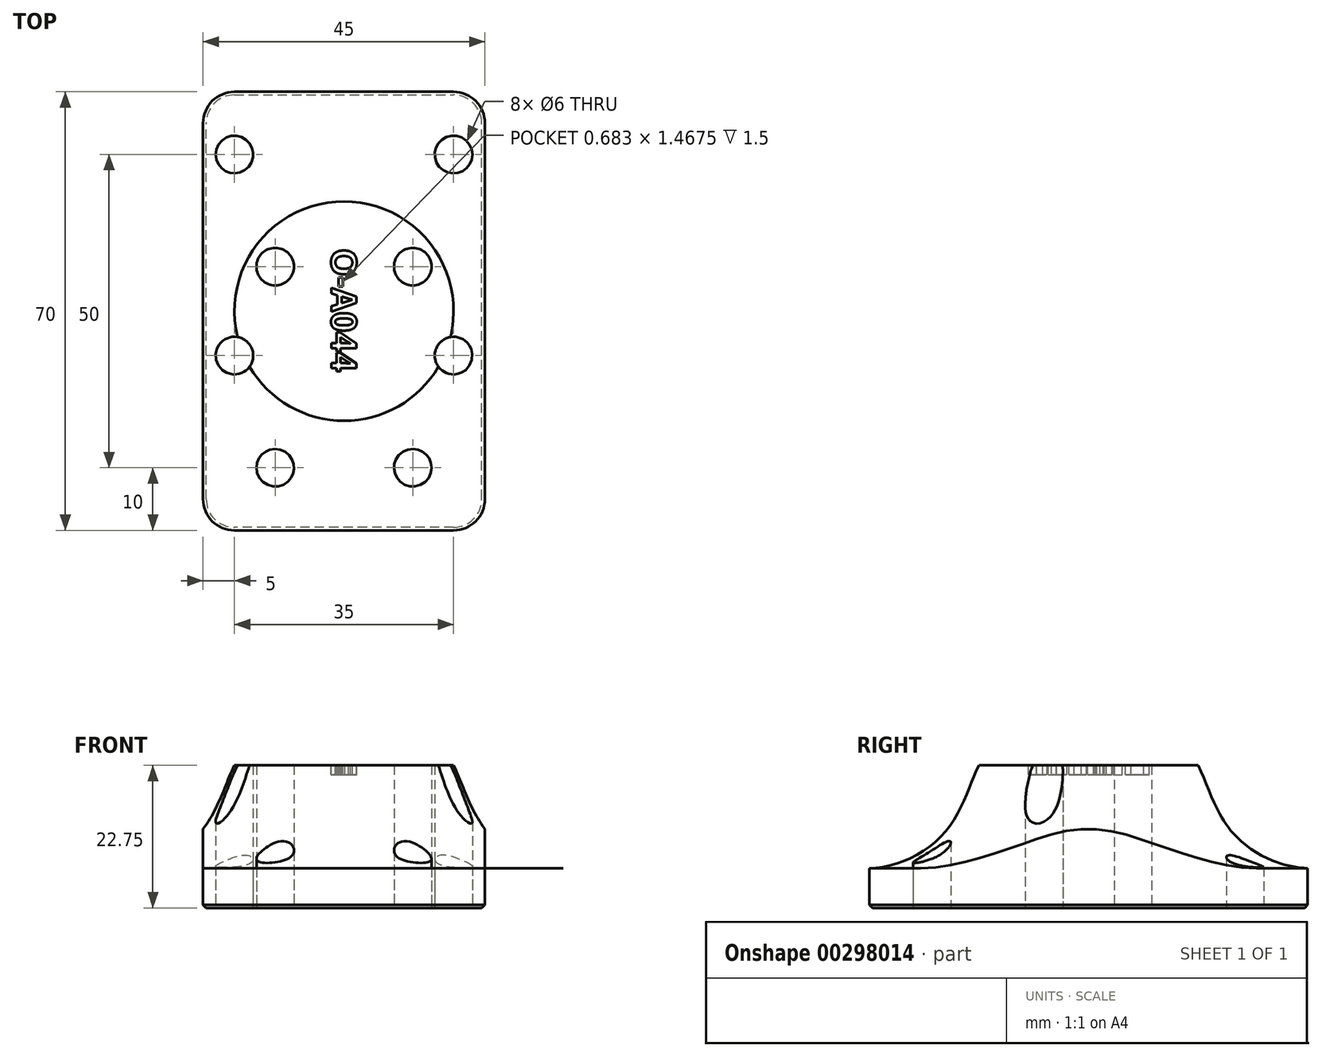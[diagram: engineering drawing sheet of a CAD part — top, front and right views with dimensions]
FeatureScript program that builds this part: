
annotation { "Feature Type Name" : "Feature", "Feature Type Description" : "" }
export const myFeature = defineFeature(function(context is Context, id is Id, definition is map)
    precondition{}
    {
        {
            var Q0;
            Q0=qCreatedBy(makeId("Top.planeOp"),FACE);
            var sketch = newSketch(context, id + "F0", { "sketchPlane" : qUnion([Q0])});
            skLineSegment(sketch, "E0.bottom", {"start": v(-22.5, 35) * mm, "end": v(22.5, 35) * mm});
            skLineSegment(sketch, "E0.top", {"start": v(-22.5, -35) * mm, "end": v(22.5, -35) * mm});
            skLineSegment(sketch, "E0.left", {"start": v(-22.5, 35) * mm, "end": v(-22.5, -35) * mm});
            skLineSegment(sketch, "E0.right", {"start": v(22.5, 35) * mm, "end": v(22.5, -35) * mm});
            skPoint(sketch, "E0.middle", {"position": v(0, 0) * mm});
            skCircle(sketch, "E1", {"center": v(-10.98, 7.1) * mm, "radius": 3 * mm});
            skCircle(sketch, "E2", {"center": v(-17.5, 25) * mm, "radius": 3 * mm});
            skLineSegment(sketch, "E3", {"start": v(-17.5, 25) * mm, "end": v(-10.98, 7.1) * mm, "construction": true});
            skCircle(sketch, "E4", {"center": v(-10.98, -25) * mm, "radius": 3 * mm});
            skCircle(sketch, "E5", {"center": v(-17.5, -7.1) * mm, "radius": 3 * mm});
            skLineSegment(sketch, "E6", {"start": v(-17.5, -7.1) * mm, "end": v(0, -7.1) * mm, "construction": true});
            skLineSegment(sketch, "E7", {"start": v(-17.5, -7.1) * mm, "end": v(-10.98, -25) * mm, "construction": true});
            skLineSegment(sketch, "E8", {"start": v(-17.5, 25) * mm, "end": v(-22.5, 25) * mm, "construction": true});
            skCircle(sketch, "E9.MirrorC", {"center": v(17.5, 25) * mm, "radius": 3 * mm});
            skCircle(sketch, "E10.MirrorC", {"center": v(10.98, 7.1) * mm, "radius": 3 * mm});
            skCircle(sketch, "E11.MirrorC", {"center": v(17.5, -7.1) * mm, "radius": 3 * mm});
            skCircle(sketch, "E12.MirrorC", {"center": v(10.98, -25) * mm, "radius": 3 * mm});
            skLineSegment(sketch, "E13", {"start": v(0, 35) * mm, "end": v(0, -35) * mm});
            skSolve(sketch);
        }
        {
            var Q0;
            {var subQ0=sQuery(id+"F0.wireOp",EDGE,"E0.left");Q0=makeQuery(id+"F0.imprint","IMPRINT",FACE,{"disambiguationData":[TD([[makeQuery(id+"F0.imprint","IMPRINT",EDGE,{"derivedFrom":subQ0}),1.0]])]});}
            extrude(context, id + "F1", {"entities" : qUnion([Q0]), "depth" : 22.75 * mm});
        }
        {
            var Q0;
            Q0=makeQuery(id+"F1.opExtrude","SWEPT_EDGE",EDGE,{"disambiguationData":[OSD([sQuery(id+"F0.wireOp",EDGE,"E0.top"),sQuery(id+"F0.wireOp",EDGE,"E0.left")])]});
            var Q1;
            Q1=makeQuery(id+"F1.opExtrude","SWEPT_EDGE",EDGE,{"disambiguationData":[OSD([sQuery(id+"F0.wireOp",EDGE,"E0.bottom"),sQuery(id+"F0.wireOp",EDGE,"E0.left")])]});
            fillet(context, id + "F2", {"entities" : qUnion([Q0, Q1]), "radius" : 5 * mm, "tangentPropagation" : true, "allowEdgeOverflow" : false});
        }
        {
            var Q0;
            Q0=makeQuery(id+"F1.opExtrude","CAP_EDGE",EDGE,{"disambiguationData":[OSD([sQuery(id+"F0.wireOp",EDGE,"E0.bottom")])],"isStart":true});
            var Q1;
            Q1=makeQuery(id+"F1.opExtrude","CAP_EDGE",EDGE,{"disambiguationData":[OSD([sQuery(id+"F0.wireOp",EDGE,"E0.left")])],"isStart":true});
            var Q2;
            Q2=makeQuery(id+"F1.opExtrude","CAP_EDGE",EDGE,{"disambiguationData":[OSD([sQuery(id+"F0.wireOp",EDGE,"E0.top")])],"isStart":true});
            chamfer(context, id + "F3", {"entities" : qUnion([Q0, Q1, Q2]), "width" : 0.5 * mm, "tangentPropagation" : true});
        }
        {
            var Q0;
            Q0=makeQuery(id+"F1.opExtrude","SWEPT_FACE",FACE,{"disambiguationData":[OSD([sQuery(id+"F0.wireOp",EDGE,"E13")])]});
            var sketch = newSketch(context, id + "F4", { "sketchPlane" : qUnion([Q0])});
            skLineSegment(sketch, "E14", {"start": v(0, 22.75) * mm, "end": v(0, 0) * mm});
            skLineSegment(sketch, "E15", {"start": v(0, 22.75) * mm, "end": v(-35, 22.75) * mm});
            skPoint(sketch, "E16", {"position": v(-17.5, 22.75) * mm});
            skFitSpline(sketch, "E17", {"points": [v(-35, 6.35) * mm, v(-23, 12) * mm, v(-17.5, 22.75) * mm], "startDerivative": vector(24.29, 0) * mm, "endDerivative": vector(9.22, 18.43) * mm});
            skLineSegment(sketch, "E18", {"start": v(0, 21.86) * mm, "end": v(0, -15.9) * mm, "construction": true});
            skLineSegment(sketch, "E19", {"start": v(-35, 6.35) * mm, "end": v(-55.86, 6.35) * mm});
            skLineSegment(sketch, "E20", {"start": v(-55.86, 6.35) * mm, "end": v(-55.86, 0) * mm});
            skLineSegment(sketch, "E21", {"start": v(-55.86, 0) * mm, "end": v(0, 0) * mm});
            skLineSegment(sketch, "E22", {"start": v(-55.86, 6.35) * mm, "end": v(-55.86, 22.75) * mm});
            skLineSegment(sketch, "E23", {"start": v(-55.86, 22.75) * mm, "end": v(-35, 22.75) * mm});
            skSolve(sketch);
        }
        {
            var Q0;
            {var subQ0=sQuery(id+"F4.wireOp",EDGE,"E19");Q0=makeQuery(id+"F4.imprint","IMPRINT",FACE,{"disambiguationData":[TD([[makeQuery(id+"F4.imprint","IMPRINT",EDGE,{"derivedFrom":subQ0}),-1.0]])]});}
            var Q1;
            {var subQ3=sQuery(id+"F4.wireOp",EDGE,"E17");Q1=makeQuery(id+"F4.imprint","IMPRINT",FACE,{"disambiguationData":[TD([[makeQuery(id+"F4.imprint","IMPRINT",EDGE,{"derivedFrom":subQ3}),1.0]])]});}
            var Q2;
            Q2=sQuery(id+"F4.wireOp",EDGE,"E18");
            revolve(context, id + "F5", {"operationType" : NewBodyOperationType.REMOVE, "entities" : qUnion([Q0, Q1]), "axis" : qUnion([Q2]), "revolveType" : RevolveType.FULL, "oppositeDirection" : true});
        }
        {
            var Q0;
            Q0=makeQuery(id+"F1.opExtrude","SWEPT_BODY",BODY,{"disambiguationData":[OSD([sQuery(id+"F0.wireOp",EDGE,"E0.bottom"),sQuery(id+"F0.wireOp",EDGE,"E0.top"),sQuery(id+"F0.wireOp",EDGE,"E0.left"),sQuery(id+"F0.wireOp",EDGE,"E1"),sQuery(id+"F0.wireOp",EDGE,"E2"),sQuery(id+"F0.wireOp",EDGE,"E4"),sQuery(id+"F0.wireOp",EDGE,"E5"),sQuery(id+"F0.wireOp",EDGE,"E13")])]});
            var Q1;
            Q1=qCreatedBy(makeId("Right.planeOp"),FACE);
            mirror(context, id + "F6", {"operationType" : NewBodyOperationType.ADD, "entities" : qUnion([Q0]), "mirrorPlane" : qUnion([Q1])});
        }
        {
            var Q0;
            {var subQ0=makeQuery(id+"F1.opExtrude","CAP_FACE",FACE,{"disambiguationData":[OSD([sQuery(id+"F0.wireOp",EDGE,"E0.bottom"),sQuery(id+"F0.wireOp",EDGE,"E0.top"),sQuery(id+"F0.wireOp",EDGE,"E0.left"),sQuery(id+"F0.wireOp",EDGE,"E1"),sQuery(id+"F0.wireOp",EDGE,"E2"),sQuery(id+"F0.wireOp",EDGE,"E4"),sQuery(id+"F0.wireOp",EDGE,"E5"),sQuery(id+"F0.wireOp",EDGE,"E13")])],"isStart":false});Q0=makeQuery(id+"F6.boolean.opBoolean","MERGE",FACE,{"derivedFrom":[subQ0,makeQuery(id+"F6.opPattern","COPY",FACE,{"derivedFrom":subQ0,"instanceName":"1"})]});}
            var sketch = newSketch(context, id + "F7", { "sketchPlane" : qUnion([Q0])});
            skText(sketch, "E24", { "text": "O-A044", "fontName": "OpenSans-Bold.ttf"});
            skPoint(sketch, "E25", {"position": v(0, 0) * mm});
            const initialGuessF7  = {"E24": [-0.00202, 0.01, 0, -1, 0.00403]};
            skSetInitialGuess(sketch, initialGuessF7);
            skSolve(sketch);
        }
        {
            var Q0;
            Q0 = qSketchRegion(id + "F7", true);
            extrude(context, id + "F8", {"entities" : qUnion([Q0]), "operationType" : NewBodyOperationType.REMOVE, "oppositeDirection" : true, "depth" : 1.5 * mm});
        }
    });
